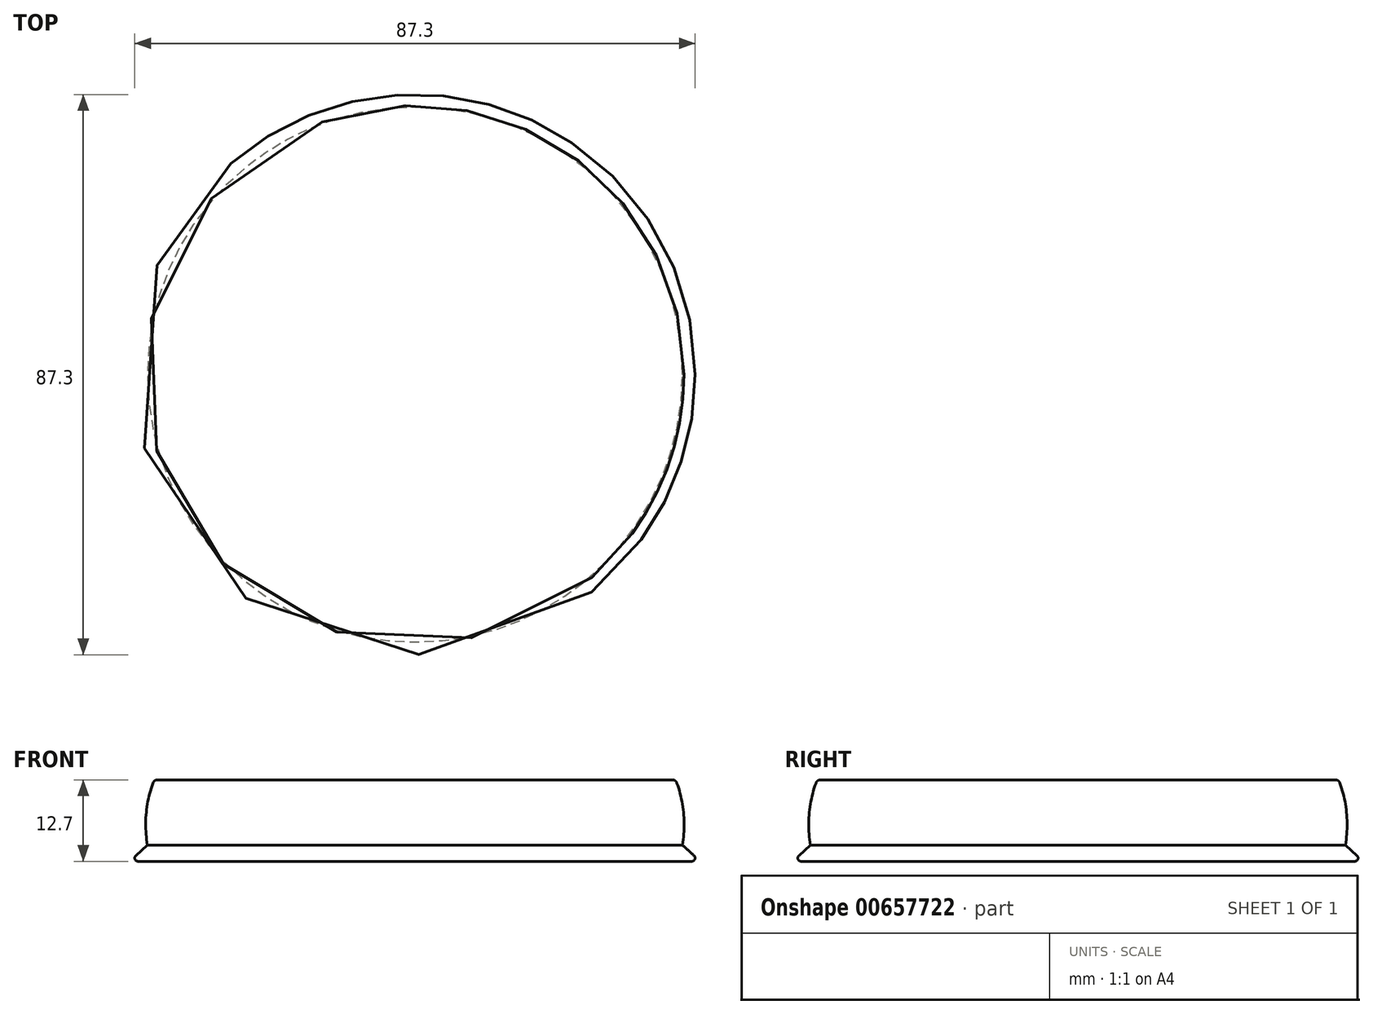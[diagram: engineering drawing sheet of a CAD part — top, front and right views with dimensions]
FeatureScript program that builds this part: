
annotation { "Feature Type Name" : "Feature", "Feature Type Description" : "" }
export const myFeature = defineFeature(function(context is Context, id is Id, definition is map)
    precondition{}
    {
        {
            var Q0;
            Q0=qCreatedBy(makeId("Front.planeOp"),FACE);
            var sketch = newSketch(context, id + "F0", { "sketchPlane" : qUnion([Q0])});
            skLineSegment(sketch, "E0", {"start": v(0, 12.7) * mm, "end": v(40.63, 12.7) * mm});
            skLineSegment(sketch, "E1.MirrorCS", {"start": v(44.45, 0) * mm, "end": v(41.67, 2.54) * mm});
            skLineSegment(sketch, "E2", {"start": v(0, 0) * mm, "end": v(44.45, 0) * mm});
            skLineSegment(sketch, "E3", {"start": v(0, 29.17) * mm, "end": v(0, -18.74) * mm, "construction": true});
            skLineSegment(sketch, "E4", {"start": v(0, 12.7) * mm, "end": v(0, 0) * mm});
            skArc(sketch, "E5", {"start": v(41.67, 2.54) * mm, "mid": v(41.84, 7.7) * mm, "end": v(40.63, 12.7) * mm});
            skSolve(sketch);
        }
        {
            var Q0;
            Q0 = qSketchRegion(id + "F0", true);
            var Q1;
            Q1=sQuery(id+"F0.wireOp",EDGE,"E3");
            revolve(context, id + "F1", {"entities" : qUnion([Q0]), "axis" : qUnion([Q1]), "revolveType" : RevolveType.FULL});
        }
        {
            var Q0;
            Q0=makeQuery(id+"F1.opRevolve","SWEPT_EDGE",EDGE,{"disambiguationData":[OSD([sQuery(id+"F0.wireOp",EDGE,"E1.MirrorCS"),sQuery(id+"F0.wireOp",EDGE,"E2")])]});
            fillet(context, id + "F2", {"entities" : qUnion([Q0]), "radius" : 0.5 * mm, "tangentPropagation" : true, "allowEdgeOverflow" : false});
        }
        {
            var Q0;
            Q0=makeQuery(id+"F1.opRevolve","SWEPT_EDGE",EDGE,{"disambiguationData":[OSD([sQuery(id+"F0.wireOp",EDGE,"E0"),sQuery(id+"F0.wireOp",EDGE,"1e057eab-d8f5-40bc-95e4-6d26b9a74a890.MirrorCS")])]});
            fillet(context, id + "F3", {"entities" : qUnion([Q0]), "radius" : 0.76 * mm, "tangentPropagation" : true, "allowEdgeOverflow" : false});
        }
    });
